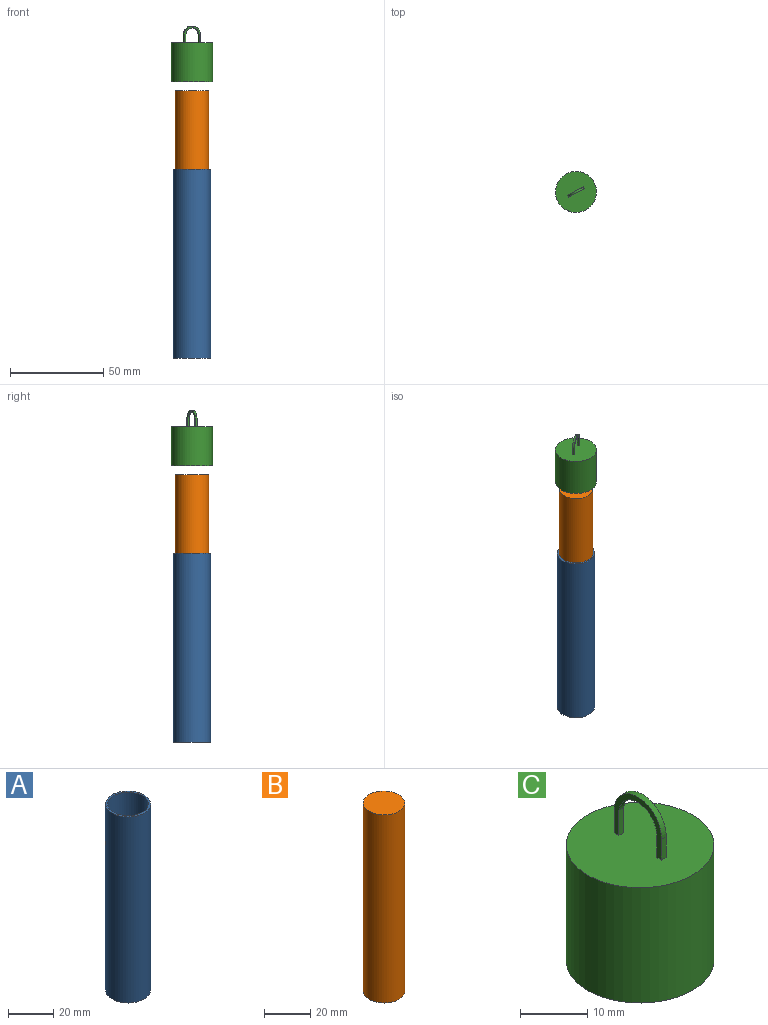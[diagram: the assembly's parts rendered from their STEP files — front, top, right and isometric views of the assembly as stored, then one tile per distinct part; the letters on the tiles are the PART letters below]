
ASSEMBLY  parts=3 mates=2
PART A: 5 faces, bbox 20x20x101 mm
  f0: cylinder r=9mm len=100mm, axis (0,0,-1), area 5654.9mm2, adj f2,f3
  f1: cylinder r=10mm len=101mm, axis (0,0,-1), area 6346mm2, adj f2,f4
  f2: plane 20x20mm, normal (0,0,1), area 59.7mm2, adj f0,f1
  f3: plane 18x18mm, normal (0,0,1), area 254.5mm2, adj f0
  f4: plane 20x20mm, normal (0,0,-1), area 314.2mm2, adj f1
PART B: 3 faces, bbox 18x18x100 mm
  f0: cylinder r=9mm len=100mm, axis (0,0,-1), area 5654.9mm2, adj f1,f2
  f1: plane 18x18mm, normal (0,0,1), area 254.5mm2, adj f0
  f2: plane 18x18mm, normal (0,0,-1), area 254.5mm2, adj f0
PART C: 23 faces, bbox 22x22x30 mm
  f0: cylinder r=10mm len=20mm, axis (0,0,-1), area 1256.6mm2, adj f2,f3
  f1: cylinder r=11mm len=22mm, axis (0,0,-1), area 1451.4mm2, adj f2,f4
  f2: plane 22x22mm, normal (0,0,-1), area 66mm2, adj f0,f1
  f3: plane 20x20mm, normal (0,0,-1), area 312.2mm2, adj f0,f14,f15,f16,f17,f18,f19,f20
  f4: plane 22x22mm, normal (0,0,1), area 378.1mm2, adj f1,f7,f8,f9,f10,f11,f12
  f5: cylinder r=4mm len=7.96mm, axis (-1,0,0), area 12.2mm2, adj f7,f8,f10,f11
  f6: cylinder r=5mm len=9.96mm, axis (-1,0,0), area 15.3mm2, adj f7,f8,f9,f12
  f7: plane 9.96x9mm, normal (-1,0,0), area 22.1mm2, adj f4,f5,f6,f9,f10,f11,f12
  f8: plane 9.96x9mm, normal (1,0,0), area 22.1mm2, adj f4,f5,f6,f9,f10,f11,f12
  f9: plane 4.65x1mm, normal (0,1,0), area 4.7mm2, adj f4,f6,f7,f8
  f10: plane 4.58x1mm, normal (0,-1,0), area 4.6mm2, adj f4,f5,f7,f8
  f11: plane 3.78x1mm, normal (0,1,0), area 3.8mm2, adj f4,f5,f7,f8
  f12: plane 3.76x1mm, normal (0,-1,0), area 3.8mm2, adj f4,f6,f7,f8
  f13: plane 1x1mm, normal (0,0,-1), area 1mm2, adj f14,f15,f16,f17
  f14: plane 1x0.18mm, normal (-1,0,0), area 0.2mm2, adj f3,f13,f16,f17
  f15: plane 1x0.18mm, normal (1,0,0), area 0.2mm2, adj f3,f13,f16,f17
  f16: plane 1x0.18mm, normal (0,1,0), area 0.2mm2, adj f3,f13,f14,f15
  f17: plane 1x0.18mm, normal (0,-1,0), area 0.2mm2, adj f3,f13,f14,f15
  f18: plane 1x0.18mm, normal (0,-1,0), area 0.2mm2, adj f3,f20,f21,f22
  f19: plane 1x0.18mm, normal (0,1,0), area 0.2mm2, adj f3,f20,f21,f22
  f20: plane 1x0.18mm, normal (1,0,0), area 0.2mm2, adj f3,f18,f19,f22
  f21: plane 1x0.18mm, normal (-1,0,0), area 0.2mm2, adj f3,f18,f19,f22
  f22: plane 1x1mm, normal (0,0,-1), area 1mm2, adj f18,f19,f20,f21
PLACE A t=(-22,-5.15,-38.68)mm fixed
PLACE B rot(axis=(0,0,-1),46.3deg) t=(-22,-5.15,3.5)mm
PLACE C rot(axis=(0,0,1),117.4deg) t=(-22,-5.15,68.21)mm
MATE cylindrical A.f0 <-> B.f0  axis (0,0,1) through (-22,-5.15,11.32)mm
MATE cylindrical C.f1 <-> A.f1  axis (0,0,-1) through (-22,-5.15,68.71)mm
